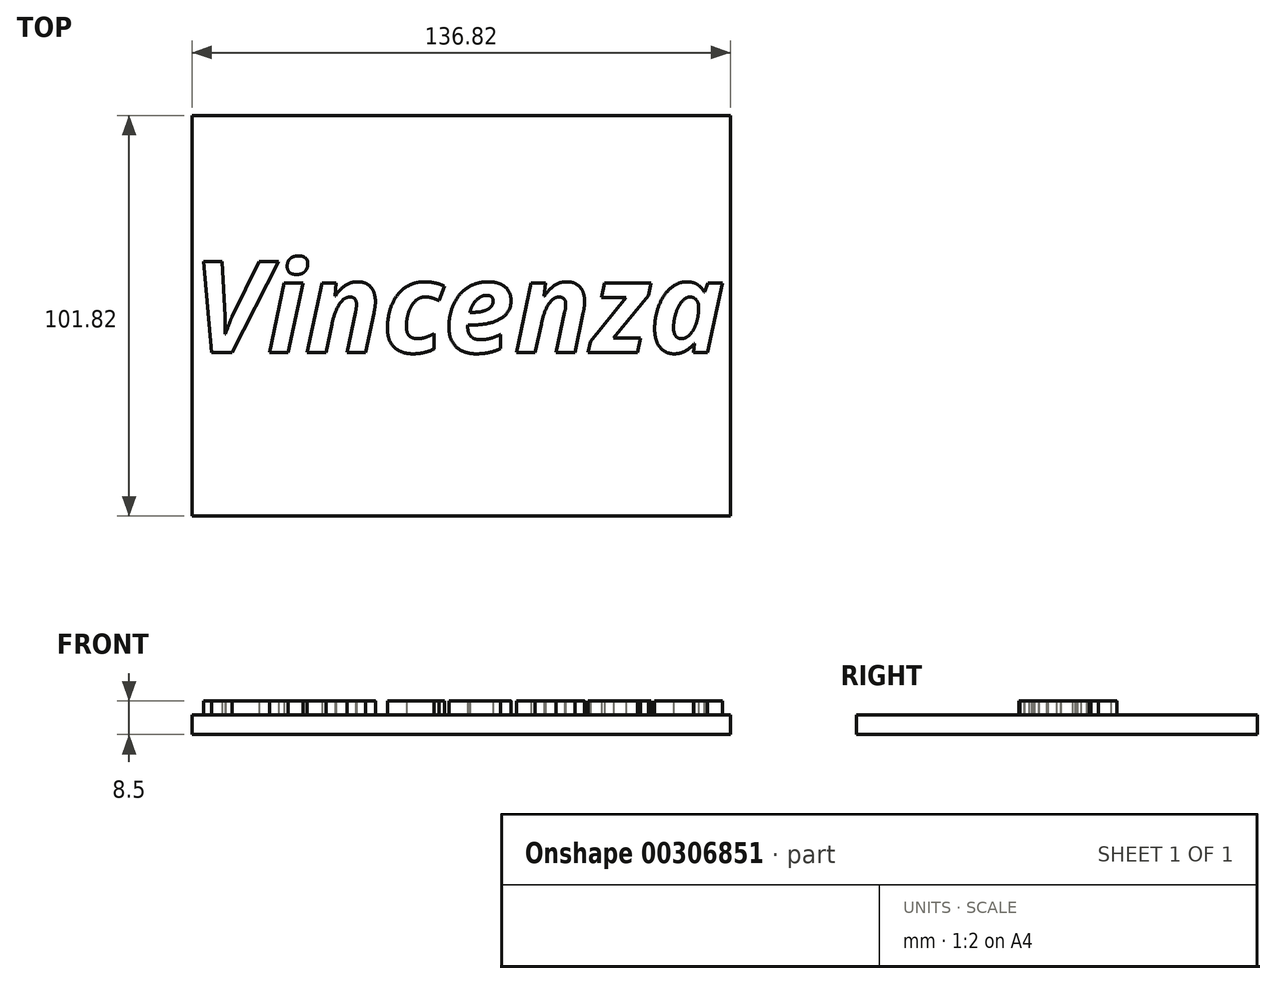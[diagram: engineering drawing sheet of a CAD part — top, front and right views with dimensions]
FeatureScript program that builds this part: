
annotation { "Feature Type Name" : "Feature", "Feature Type Description" : "" }
export const myFeature = defineFeature(function(context is Context, id is Id, definition is map)
    precondition{}
    {
        {
            var Q0;
            Q0=qCreatedBy(makeId("Top.planeOp"),FACE);
            var sketch = newSketch(context, id + "F0", { "sketchPlane" : qUnion([Q0])});
            skLineSegment(sketch, "E0.bottom", {"start": v(68.4, -50.91) * mm, "end": v(-68.4, -50.91) * mm});
            skLineSegment(sketch, "E0.top", {"start": v(68.4, 50.91) * mm, "end": v(-68.4, 50.91) * mm});
            skLineSegment(sketch, "E0.left", {"start": v(68.4, -50.91) * mm, "end": v(68.4, 50.91) * mm});
            skLineSegment(sketch, "E0.right", {"start": v(-68.4, -50.91) * mm, "end": v(-68.4, 50.91) * mm});
            skPoint(sketch, "E0.middle", {"position": v(0, 0) * mm});
            skSolve(sketch);
        }
        {
            var Q0;
            Q0=makeQuery(id+"F0.imprint","IMPRINT",FACE,{"disambiguationData":[TD([[makeQuery(id+"F0.imprint","IMPRINT",EDGE,{"derivedFrom":sQuery(id+"F0.wireOp",EDGE,"E0.bottom")}),-1.0]])]});
            extrude(context, id + "F1", {"entities" : qUnion([Q0]), "depth" : 5 * mm});
        }
        {
            var Q0;
            Q0=makeQuery(id+"F1.opExtrude","CAP_FACE",FACE,{"disambiguationData":[OSD([sQuery(id+"F0.wireOp",EDGE,"E0.bottom"),sQuery(id+"F0.wireOp",EDGE,"E0.top"),sQuery(id+"F0.wireOp",EDGE,"E0.left"),sQuery(id+"F0.wireOp",EDGE,"E0.right")])],"isStart":false});
            var sketch = newSketch(context, id + "F2", { "sketchPlane" : qUnion([Q0])});
            skText(sketch, "E1", { "text": "Vincenza", "fontName": "OpenSans-BoldItalic.ttf"});
            const initialGuessF2  = {"E1": [-0.0684, -0.00936, 1, 0, 0.02328]};
            skSetInitialGuess(sketch, initialGuessF2);
            skSolve(sketch);
        }
        {
            var Q0;
            Q0 = qSketchRegion(id + "F2", true);
            extrude(context, id + "F3", {"entities" : qUnion([Q0]), "operationType" : NewBodyOperationType.ADD, "depth" : 3.5 * mm});
        }
    });
